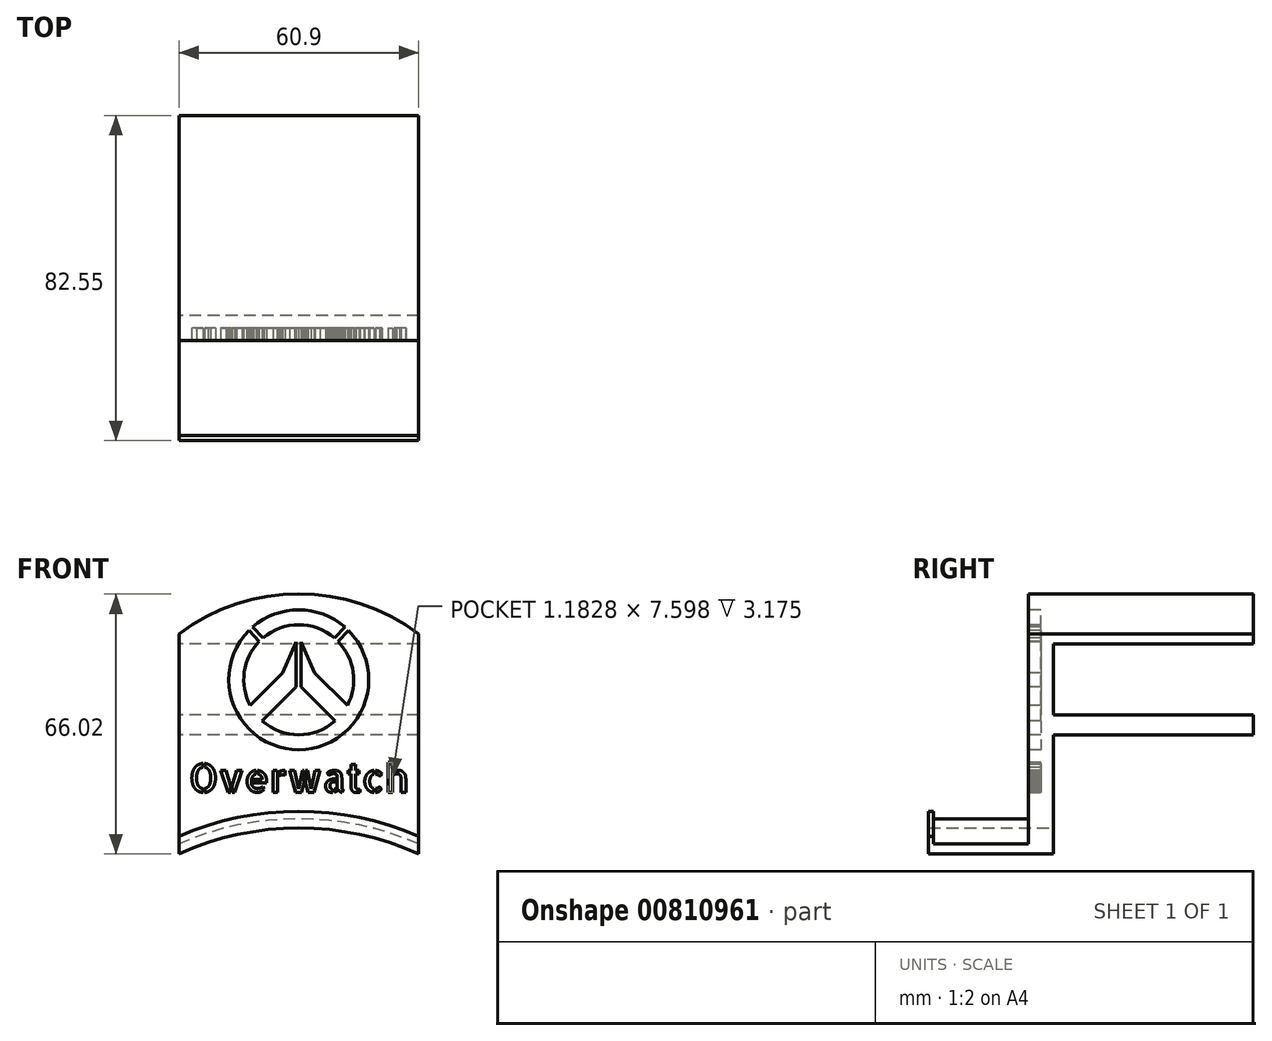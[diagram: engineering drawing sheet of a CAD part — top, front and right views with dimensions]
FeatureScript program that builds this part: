
annotation { "Feature Type Name" : "Feature", "Feature Type Description" : "" }
export const myFeature = defineFeature(function(context is Context, id is Id, definition is map)
    precondition{}
    {
        {
            var Q0;
            Q0=qCreatedBy(makeId("Front.planeOp"),FACE);
            var sketch = newSketch(context, id + "F0", { "sketchPlane" : qUnion([Q0])});
            skCircle(sketch, "E0", {"center": v(0, -76.2) * mm, "radius": 76.2 * mm, "construction": true});
            skLineSegment(sketch, "E1", {"start": v(0, -6.35) * mm, "end": v(0, 0) * mm});
            skArc(sketch, "E2", {"start": v(30.45, -6.35) * mm, "mid": v(0, 0) * mm, "end": v(-30.45, -6.35) * mm});
            skLineSegment(sketch, "E3", {"start": v(-30.45, -6.35) * mm, "end": v(-30.45, 44.45) * mm});
            skLineSegment(sketch, "E4", {"start": v(30.45, -6.35) * mm, "end": v(30.45, 44.45) * mm});
            skArc(sketch, "E5", {"start": v(30.45, 44.45) * mm, "mid": v(0, 54.6) * mm, "end": v(-30.45, 44.45) * mm});
            skLineSegment(sketch, "E6", {"start": v(-30.45, -6.35) * mm, "end": v(-30.45, -8.9) * mm});
            skLineSegment(sketch, "E7", {"start": v(30.45, -6.35) * mm, "end": v(30.45, -8.9) * mm});
            skArc(sketch, "E8", {"start": v(30.45, -8.89) * mm, "mid": v(0, -2.32) * mm, "end": v(-30.45, -8.89) * mm});
            skLineSegment(sketch, "E9", {"start": v(-30.45, 44.45) * mm, "end": v(-30.45, 46.99) * mm});
            skLineSegment(sketch, "E10", {"start": v(30.45, 44.45) * mm, "end": v(30.45, 46.99) * mm});
            skArc(sketch, "E11", {"start": v(30.45, 47) * mm, "mid": v(0, 57.13) * mm, "end": v(-30.45, 47) * mm});
            skLineSegment(sketch, "E12", {"start": v(-30.45, 44.45) * mm, "end": v(30.45, 44.45) * mm});
            skLineSegment(sketch, "E13", {"start": v(-30.45, 19.05) * mm, "end": v(30.45, 19.05) * mm, "construction": true});
            skLineSegment(sketch, "E14", {"start": v(0, 19.05) * mm, "end": v(0, 26.67) * mm});
            skCircle(sketch, "E15", {"center": v(0, 26.67) * mm, "radius": 17.78 * mm, "construction": true});
            skCircle(sketch, "E16", {"center": v(0, 26.67) * mm, "radius": 13.97 * mm, "construction": true});
            skSolve(sketch);
        }
        {
            var Q0;
            {var subQ1=sQuery(id+"F0.wireOp",EDGE,"E3");Q0=makeQuery(id+"F0.imprint","IMPRINT",FACE,{"disambiguationData":[TD([[makeQuery(id+"F0.imprint","IMPRINT",EDGE,{"derivedFrom":subQ1}),-1.0]])]});}
            var Q1;
            Q1=makeQuery(id+"F0.imprint","IMPRINT",FACE,{"disambiguationData":[TD([[makeQuery(id+"F0.imprint","IMPRINT",EDGE,{"derivedFrom":sQuery(id+"F0.wireOp",EDGE,"E5")}),1.0]])]});
            extrude(context, id + "F1", {"entities" : qUnion([Q0, Q1]), "depth" : 6.35 * mm, "offsetDistance" : 25.4 * mm});
        }
        {
            var Q0;
            {var subQ5=sQuery(id+"F0.wireOp",EDGE,"E7");Q0=makeQuery(id+"F0.imprint","IMPRINT",FACE,{"disambiguationData":[TD([[makeQuery(id+"F0.imprint","IMPRINT",EDGE,{"derivedFrom":subQ5}),-1.0]])]});}
            var Q1;
            {var subQ5=sQuery(id+"F0.wireOp",EDGE,"E6");Q1=makeQuery(id+"F0.imprint","IMPRINT",FACE,{"disambiguationData":[TD([[makeQuery(id+"F0.imprint","IMPRINT",EDGE,{"derivedFrom":subQ5}),1.0]])]});}
            extrude(context, id + "F2", {"entities" : qUnion([Q0, Q1]), "operationType" : NewBodyOperationType.ADD, "depth" : 31.75 * mm, "offsetDistance" : 25.4 * mm});
        }
        {
            var Q0;
            Q0=makeQuery(id+"F0.imprint","IMPRINT",FACE,{"disambiguationData":[TD([[makeQuery(id+"F0.imprint","IMPRINT",EDGE,{"derivedFrom":sQuery(id+"F0.wireOp",EDGE,"E5")}),-1.0]])]});
            var Q1;
            Q1=makeQuery(id+"F0.imprint","IMPRINT",FACE,{"disambiguationData":[TD([[makeQuery(id+"F0.imprint","IMPRINT",EDGE,{"derivedFrom":sQuery(id+"F0.wireOp",EDGE,"E5")}),1.0]])]});
            var Q2;
            Q2=makeQuery(id+"F1.opExtrude","CAP_FACE",FACE,{"disambiguationData":[OSD([sQuery(id+"F0.wireOp",EDGE,"E2"),sQuery(id+"F0.wireOp",EDGE,"E3"),sQuery(id+"F0.wireOp",EDGE,"E4"),sQuery(id+"F0.wireOp",EDGE,"E5")])],"isStart":false});
            extrude(context, id + "F3", {"entities" : qUnion([Q0, Q1]), "operationType" : NewBodyOperationType.ADD, "endBound" : BoundingType.UP_TO_SURFACE, "depth" : 25.4 * mm, "endBoundEntityFace" : qUnion([Q2]), "offsetDistance" : 25.4 * mm, "hasSecondDirection" : true, "secondDirectionOppositeDirection" : true, "secondDirectionDepth" : 50.8 * mm});
        }
        {
            var Q0;
            {var subQ0=sQuery(id+"F0.wireOp",EDGE,"E5");var subQ1=sQuery(id+"F0.wireOp",EDGE,"E4");var subQ2=sQuery(id+"F0.wireOp",EDGE,"E3");var subQ3=sQuery(id+"F0.wireOp",EDGE,"E2");Q0=makeQuery(id+"F3.boolean.opBoolean","MERGE",FACE,{"derivedFrom":[makeQuery(id+"F1.opExtrude","CAP_FACE",FACE,{"disambiguationData":[OSD([subQ3,subQ2,subQ1,subQ0])],"isStart":false}),makeQuery(id+"F3.opExtrude","CAP_FACE",FACE,{"disambiguationData":[OSD([subQ3,subQ2,subQ1,subQ0])],"isStart":false})]});}
            var sketch = newSketch(context, id + "F4", { "sketchPlane" : qUnion([Q0])});
            skLineSegment(sketch, "E17.0.0", {"start": v(30.45, -6.35) * mm, "end": v(30.45, 46.99) * mm});
            skArc(sketch, "E17.0.1", {"start": v(30.45, 47) * mm, "mid": v(0, 57.13) * mm, "end": v(-30.45, 47) * mm});
            skLineSegment(sketch, "E17.0.2", {"start": v(-30.45, 47) * mm, "end": v(-30.45, -6.35) * mm});
            skArc(sketch, "E17.0.3", {"start": v(-30.45, -6.35) * mm, "mid": v(0, 0) * mm, "end": v(30.45, -6.35) * mm});
            skLineSegment(sketch, "E18", {"start": v(0, 69.22) * mm, "end": v(0, -34.38) * mm, "construction": true});
            skLineSegment(sketch, "E19", {"start": v(-30.45, 16.21) * mm, "end": v(31.03, 16.21) * mm, "construction": true});
            skLineSegment(sketch, "E20", {"start": v(-30.45, 6.76) * mm, "end": v(-27.91, 6.76) * mm, "construction": true});
            skLineSegment(sketch, "E21.MirrorCS", {"start": v(30.45, 6.76) * mm, "end": v(27.91, 6.76) * mm, "construction": true});
            skText(sketch, "E22", { "text": "Overwatch", "fontName": "AllertaStencil-Regular.ttf"});
            skPoint(sketch, "E22.firstSnap0", {"position": v(0, 8.89) * mm});
            skArc(sketch, "E23.0", {"start": v(-10.03, 45.06) * mm, "mid": v(-13.83, 37.32) * mm, "end": v(-12.36, 28.83) * mm});
            skArc(sketch, "E24.0", {"start": v(-12.65, 47.84) * mm, "mid": v(0, 17.56) * mm, "end": v(12.65, 47.84) * mm});
            skLineSegment(sketch, "E25", {"start": v(-9.1, 45.94) * mm, "end": v(-11.72, 48.71) * mm});
            skLineSegment(sketch, "E26", {"start": v(-10.03, 45.06) * mm, "end": v(-12.65, 47.84) * mm});
            skLineSegment(sketch, "E27.MirrorCS", {"start": v(9.1, 45.94) * mm, "end": v(11.72, 48.71) * mm});
            skLineSegment(sketch, "E28.MirrorCS", {"start": v(10.03, 45.06) * mm, "end": v(12.65, 47.84) * mm});
            skLineSegment(sketch, "E29", {"start": v(-9.26, 24.88) * mm, "end": v(-0.64, 33.5) * mm});
            skLineSegment(sketch, "E30", {"start": v(-0.64, 33.5) * mm, "end": v(-0.64, 44.94) * mm});
            skLineSegment(sketch, "E31", {"start": v(-0.64, 44.94) * mm, "end": v(-4.06, 37.13) * mm});
            skLineSegment(sketch, "E32.MirrorCS", {"start": v(0.64, 44.94) * mm, "end": v(4.06, 37.13) * mm});
            skLineSegment(sketch, "E33.MirrorCS", {"start": v(0.64, 33.5) * mm, "end": v(0.64, 44.94) * mm});
            skLineSegment(sketch, "E34.MirrorCS", {"start": v(9.26, 24.88) * mm, "end": v(0.64, 33.5) * mm});
            skLineSegment(sketch, "E35", {"start": v(-12.36, 28.83) * mm, "end": v(-4.06, 37.13) * mm});
            skLineSegment(sketch, "E36.MirrorCS", {"start": v(12.36, 28.83) * mm, "end": v(4.06, 37.13) * mm});
            skArc(sketch, "E37.trimOffspring", {"start": v(-9.26, 24.88) * mm, "mid": v(0, 21.37) * mm, "end": v(9.26, 24.88) * mm});
            skArc(sketch, "E38.trimOffspring", {"start": v(12.36, 28.83) * mm, "mid": v(13.83, 37.32) * mm, "end": v(10.03, 45.06) * mm});
            skArc(sketch, "E39.trimOffspring", {"start": v(9.1, 45.94) * mm, "mid": v(0, 49.31) * mm, "end": v(-9.1, 45.94) * mm});
            skArc(sketch, "E40.trimOffspring", {"start": v(11.72, 48.71) * mm, "mid": v(0, 53.12) * mm, "end": v(-11.72, 48.71) * mm});
            const initialGuessF4  = {"E22": [-0.02791, 0.00676, 1, 0, 0.00721]};
            skSetInitialGuess(sketch, initialGuessF4);
            skSolve(sketch);
        }
        {
            var Q0;
            Q0=makeQuery(id+"F4.imprint","IMPRINT",FACE,{"disambiguationData":[TD([[makeQuery(id+"F4.imprint","IMPRINT",EDGE,{"derivedFrom":sQuery(id+"F4.wireOp",EDGE,"E25")}),-1.0]])]});
            var Q1;
            Q1=makeQuery(id+"F4.imprint","IMPRINT",FACE,{"disambiguationData":[TD([[makeQuery(id+"F4.imprint","IMPRINT",EDGE,{"derivedFrom":sQuery(id+"F4.wireOp",EDGE,"E23.0")}),-1.0]])]});
            var Q2;
            Q2=makeQuery(id+"F4.imprint","IMPRINT",FACE,{"disambiguationData":[TD([[makeQuery(id+"F4.imprint","IMPRINT",EDGE,{"derivedFrom":sQuery(id+"F4.wireOp",EDGE,"E22.sketch_text.stroke-0")}),-1.0]])]});
            var Q3;
            Q3=makeQuery(id+"F4.imprint","IMPRINT",FACE,{"disambiguationData":[TD([[makeQuery(id+"F4.imprint","IMPRINT",EDGE,{"derivedFrom":sQuery(id+"F4.wireOp",EDGE,"E22.sketch_text.stroke-18")}),-1.0]])]});
            var Q4;
            Q4=makeQuery(id+"F4.imprint","IMPRINT",FACE,{"disambiguationData":[TD([[makeQuery(id+"F4.imprint","IMPRINT",EDGE,{"derivedFrom":sQuery(id+"F4.wireOp",EDGE,"E22.sketch_text.stroke-36")}),-1.0]])]});
            var Q5;
            Q5=makeQuery(id+"F4.imprint","IMPRINT",FACE,{"disambiguationData":[TD([[makeQuery(id+"F4.imprint","IMPRINT",EDGE,{"derivedFrom":sQuery(id+"F4.wireOp",EDGE,"E22.sketch_text.stroke-41")}),-1.0]])]});
            var Q6;
            Q6=makeQuery(id+"F4.imprint","IMPRINT",FACE,{"disambiguationData":[TD([[makeQuery(id+"F4.imprint","IMPRINT",EDGE,{"derivedFrom":sQuery(id+"F4.wireOp",EDGE,"E22.sketch_text.stroke-59")}),-1.0]])]});
            var Q7;
            Q7=makeQuery(id+"F4.imprint","IMPRINT",FACE,{"disambiguationData":[TD([[makeQuery(id+"F4.imprint","IMPRINT",EDGE,{"derivedFrom":sQuery(id+"F4.wireOp",EDGE,"E22.sketch_text.stroke-46")}),-1.0]])]});
            var Q8;
            Q8=makeQuery(id+"F4.imprint","IMPRINT",FACE,{"disambiguationData":[TD([[makeQuery(id+"F4.imprint","IMPRINT",EDGE,{"derivedFrom":sQuery(id+"F4.wireOp",EDGE,"E22.sketch_text.stroke-83")}),-1.0]])]});
            var Q9;
            Q9=makeQuery(id+"F4.imprint","IMPRINT",FACE,{"disambiguationData":[TD([[makeQuery(id+"F4.imprint","IMPRINT",EDGE,{"derivedFrom":sQuery(id+"F4.wireOp",EDGE,"E22.sketch_text.stroke-90")}),-1.0]])]});
            var Q10;
            {var subQ0=sQuery(id+"F0.wireOp",EDGE,"E2");Q10=makeQuery(id+"F2.boolean.opBoolean","MERGE",FACE,{"derivedFrom":[makeQuery(id+"F1.opExtrude","CAP_FACE",FACE,{"disambiguationData":[OSD([subQ0,sQuery(id+"F0.wireOp",EDGE,"E3"),sQuery(id+"F0.wireOp",EDGE,"E4"),sQuery(id+"F0.wireOp",EDGE,"E5")])],"isStart":true}),makeQuery(id+"F2.opExtrude","CAP_FACE",FACE,{"disambiguationData":[OSD([subQ0,sQuery(id+"F0.wireOp",EDGE,"E6"),sQuery(id+"F0.wireOp",EDGE,"E7"),sQuery(id+"F0.wireOp",EDGE,"E8")])],"isStart":true})]});}
            var Q11;
            Q11=makeQuery(id+"F4.imprint","IMPRINT",FACE,{"disambiguationData":[TD([[makeQuery(id+"F4.imprint","IMPRINT",EDGE,{"derivedFrom":sQuery(id+"F4.wireOp",EDGE,"E22.sketch_text.stroke-105")}),-1.0]])]});
            var Q12;
            Q12=makeQuery(id+"F4.imprint","IMPRINT",FACE,{"disambiguationData":[TD([[makeQuery(id+"F4.imprint","IMPRINT",EDGE,{"derivedFrom":sQuery(id+"F4.wireOp",EDGE,"E22.sketch_text.stroke-97")}),-1.0]])]});
            var Q13;
            Q13=makeQuery(id+"F4.imprint","IMPRINT",FACE,{"disambiguationData":[TD([[makeQuery(id+"F4.imprint","IMPRINT",EDGE,{"derivedFrom":sQuery(id+"F4.wireOp",EDGE,"E22.sketch_text.stroke-132")}),-1.0]])]});
            var Q14;
            Q14=makeQuery(id+"F4.imprint","IMPRINT",FACE,{"disambiguationData":[TD([[makeQuery(id+"F4.imprint","IMPRINT",EDGE,{"derivedFrom":sQuery(id+"F4.wireOp",EDGE,"E22.sketch_text.stroke-113")}),-1.0]])]});
            var Q15;
            Q15=makeQuery(id+"F4.imprint","IMPRINT",FACE,{"disambiguationData":[TD([[makeQuery(id+"F4.imprint","IMPRINT",EDGE,{"derivedFrom":sQuery(id+"F4.wireOp",EDGE,"E22.sketch_text.stroke-168")}),-1.0]])]});
            var Q16;
            Q16=makeQuery(id+"F4.imprint","IMPRINT",FACE,{"disambiguationData":[TD([[makeQuery(id+"F4.imprint","IMPRINT",EDGE,{"derivedFrom":sQuery(id+"F4.wireOp",EDGE,"E22.sketch_text.stroke-205")}),-1.0]])]});
            var Q17;
            Q17=makeQuery(id+"F4.imprint","IMPRINT",FACE,{"disambiguationData":[TD([[makeQuery(id+"F4.imprint","IMPRINT",EDGE,{"derivedFrom":sQuery(id+"F4.wireOp",EDGE,"E22.sketch_text.stroke-193")}),-1.0]])]});
            var Q18;
            Q18=makeQuery(id+"F4.imprint","IMPRINT",FACE,{"disambiguationData":[TD([[makeQuery(id+"F4.imprint","IMPRINT",EDGE,{"derivedFrom":sQuery(id+"F4.wireOp",EDGE,"E22.sketch_text.stroke-199")}),-1.0]])]});
            var Q19;
            Q19=makeQuery(id+"F4.imprint","IMPRINT",FACE,{"disambiguationData":[TD([[makeQuery(id+"F4.imprint","IMPRINT",EDGE,{"derivedFrom":sQuery(id+"F4.wireOp",EDGE,"E22.sketch_text.stroke-221")}),-1.0]])]});
            var Q20;
            Q20=makeQuery(id+"F4.imprint","IMPRINT",FACE,{"disambiguationData":[TD([[makeQuery(id+"F4.imprint","IMPRINT",EDGE,{"derivedFrom":sQuery(id+"F4.wireOp",EDGE,"E22.sketch_text.stroke-225")}),-1.0]])]});
            extrude(context, id + "F5", {"entities" : qUnion([Q0, Q1, Q2, Q3, Q4, Q5, Q6, Q7, Q8, Q9, Q10, Q11, Q12, Q13, Q14, Q15, Q16, Q17, Q18, Q19, Q20]), "operationType" : NewBodyOperationType.REMOVE, "oppositeDirection" : true, "depth" : 3.17 * mm, "offsetDistance" : 25.4 * mm});
        }
        {
            var Q0;
            {var subQ0=sQuery(id+"F0.wireOp",EDGE,"E2");Q0=makeQuery(id+"F2.boolean.opBoolean","MERGE",FACE,{"derivedFrom":[makeQuery(id+"F1.opExtrude","CAP_FACE",FACE,{"disambiguationData":[OSD([subQ0,sQuery(id+"F0.wireOp",EDGE,"E3"),sQuery(id+"F0.wireOp",EDGE,"E4"),sQuery(id+"F0.wireOp",EDGE,"E5")])],"isStart":true}),makeQuery(id+"F2.opExtrude","CAP_FACE",FACE,{"disambiguationData":[OSD([subQ0,sQuery(id+"F0.wireOp",EDGE,"E6"),sQuery(id+"F0.wireOp",EDGE,"E7"),sQuery(id+"F0.wireOp",EDGE,"E8")])],"isStart":true})]});}
            var sketch = newSketch(context, id + "F6", { "sketchPlane" : qUnion([Q0])});
            skLineSegment(sketch, "E41.0", {"start": v(-30.45, 44.45) * mm, "end": v(30.45, 44.45) * mm});
            skLineSegment(sketch, "E42", {"start": v(-30.45, 44.45) * mm, "end": v(-30.45, 26.42) * mm});
            skLineSegment(sketch, "E43", {"start": v(30.45, 44.45) * mm, "end": v(30.45, 26.42) * mm});
            skLineSegment(sketch, "E44", {"start": v(-30.45, 26.42) * mm, "end": v(30.45, 26.42) * mm});
            skLineSegment(sketch, "E45", {"start": v(-30.45, 26.42) * mm, "end": v(-30.45, 21.34) * mm});
            skLineSegment(sketch, "E46", {"start": v(-30.45, 21.34) * mm, "end": v(30.45, 21.34) * mm});
            skLineSegment(sketch, "E47", {"start": v(30.45, 21.34) * mm, "end": v(30.45, 26.42) * mm});
            skSolve(sketch);
        }
        {
            var Q0;
            Q0=makeQuery(id+"F6.imprint","IMPRINT",FACE,{"disambiguationData":[TD([[makeQuery(id+"F6.imprint","IMPRINT",EDGE,{"derivedFrom":sQuery(id+"F6.wireOp",EDGE,"E44")}),-1.0]])]});
            var Q1;
            Q1=makeQuery(id+"F3.opExtrude","CAP_FACE",FACE,{"disambiguationData":[OSD([sQuery(id+"F0.wireOp",EDGE,"E9"),sQuery(id+"F0.wireOp",EDGE,"E10"),sQuery(id+"F0.wireOp",EDGE,"E11"),sQuery(id+"F0.wireOp",EDGE,"E12")])],"isStart":true});
            extrude(context, id + "F7", {"entities" : qUnion([Q0]), "operationType" : NewBodyOperationType.ADD, "endBound" : BoundingType.UP_TO_SURFACE, "depth" : 25.4 * mm, "endBoundEntityFace" : qUnion([Q1]), "offsetDistance" : 25.4 * mm});
        }
        {
            var Q0;
            Q0=makeQuery(id+"F2.opExtrude","CAP_FACE",FACE,{"disambiguationData":[OSD([sQuery(id+"F0.wireOp",EDGE,"E2"),sQuery(id+"F0.wireOp",EDGE,"E6"),sQuery(id+"F0.wireOp",EDGE,"E7"),sQuery(id+"F0.wireOp",EDGE,"E8")])],"isStart":false});
            var sketch = newSketch(context, id + "F8", { "sketchPlane" : qUnion([Q0])});
            skLineSegment(sketch, "E48", {"start": v(-30.45, -6.35) * mm, "end": v(-30.45, -4.44) * mm});
            skLineSegment(sketch, "E49", {"start": v(30.45, -6.35) * mm, "end": v(30.45, -4.44) * mm});
            skArc(sketch, "E50.0", {"start": v(30.45, -6.35) * mm, "mid": v(0, 0) * mm, "end": v(-30.45, -6.35) * mm});
            skArc(sketch, "E51", {"start": v(30.45, -4.44) * mm, "mid": v(0, 1.9) * mm, "end": v(-30.45, -4.44) * mm});
            skSolve(sketch);
        }
        {
            var Q0;
            Q0=makeQuery(id+"F8.imprint","IMPRINT",FACE,{"disambiguationData":[TD([[makeQuery(id+"F8.imprint","IMPRINT",EDGE,{"derivedFrom":sQuery(id+"F8.wireOp",EDGE,"E48")}),-1.0]])]});
            extrude(context, id + "F9", {"entities" : qUnion([Q0]), "operationType" : NewBodyOperationType.ADD, "oppositeDirection" : true, "depth" : 1.27 * mm, "offsetDistance" : 25.4 * mm});
        }
    });
